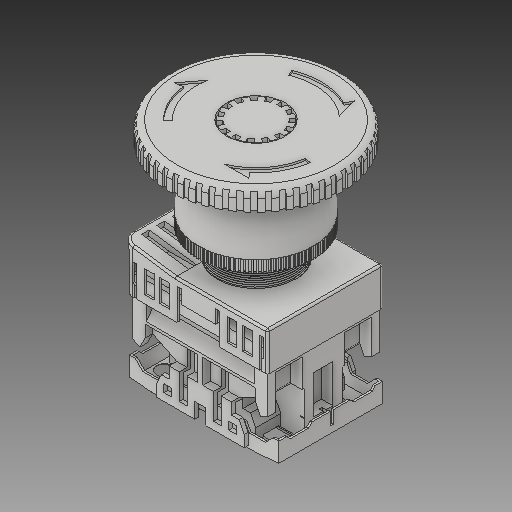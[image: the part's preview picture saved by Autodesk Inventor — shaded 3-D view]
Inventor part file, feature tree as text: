
AUTODESK INVENTOR PART (.ipt)
format: ipt  version: 2018 (Build 220112000, 112)  size: 1,929,728 bytes
history: native  units: mm
features: fillet x2, other x2, mirror x2
ambient origin geometry x8: Origin, YZ Plane, XZ Plane, XY Plane, X Axis, Y Axis, Z Axis, Center Point
bodies: Solid1 (feature_tree), Solid2 (feature_tree), Solid3 (feature_tree), Solid4 (feature_tree), Solid5 (feature_tree), Solid6 (feature_tree)
feature tree (6):
  fillet  "Fillet4"  [1 undecoded]
  fillet  "Fillet3"  [1 undecoded]
  other  "Cut-Extrude21[1]"
  mirror  "Mirror22[1]"
  mirror  "Mirror22[2]"
  other  "Cut-Extrude25"
note: 2 required parameter values undecoded (feature->parameter linkage not recoverable at this tier; creation-order binding heuristic only, values carry confidence <= 0.55)
